FCSTD DOCUMENT  (FreeCAD 1.0R38643 (Git))
Label: Acryl01
License: All rights reserved
LicenseURL: https://en.wikipedia.org/wiki/All_rights_reserved
objects: Sketcher::SketchObject×1, PartDesign::Body×1
note: 3 computed .brp shape members not serialized (recipe doc carries the construction recipe); baked Part::Feature solids carry a one-line shape summary decoded from their .brp

FEATURE [Sketcher::SketchObject] Sketch
  ArcFitTolerance = 1e-06
  AttachmentSupport = -> [XY_Plane]
  FullyConstrained = false
  MakeInternals = false
  MapMode = 5
  sketch-geometry (21):
    g0: LineSegment StartX=-152.14 StartY=63 StartZ=0 EndX=-152.14 EndY=12 EndZ=0
    g1: LineSegment StartX=-140.14 StartY=0 StartZ=0 EndX=5.86047 EndY=0 EndZ=0
    g2: LineSegment StartX=17.8605 StartY=12 StartZ=0 EndX=17.8605 EndY=63 EndZ=0
    g3: LineSegment StartX=5.86047 StartY=75 StartZ=0 EndX=-140.14 EndY=75 EndZ=0
    g4: ArcOfCircle CenterX=-140.14 CenterY=63 CenterZ=0 NormalX=0 NormalY=0 NormalZ=1 AngleXU=0 Radius=12 StartAngle=1.5708 EndAngle=3.14159
    g5: ArcOfCircle CenterX=-140.14 CenterY=12 CenterZ=0 NormalX=0 NormalY=0 NormalZ=1 AngleXU=0 Radius=12 StartAngle=3.14159 EndAngle=4.71239
    g6: ArcOfCircle CenterX=5.86047 CenterY=12 CenterZ=0 NormalX=0 NormalY=0 NormalZ=1 AngleXU=0 Radius=12 StartAngle=4.71239 EndAngle=6.28319
    g7: ArcOfCircle CenterX=5.86047 CenterY=63 CenterZ=0 NormalX=0 NormalY=0 NormalZ=1 AngleXU=0 Radius=12 StartAngle=2e-16 EndAngle=1.5708
    g8: GeomPoint [constr] X=-152.14 Y=75 Z=0
    g9: GeomPoint [constr] X=17.8605 Y=0 Z=0
    g10: Circle CenterX=5.96219 CenterY=55.25 CenterZ=0 NormalX=0 NormalY=0 NormalZ=1 AngleXU=0 Radius=1.5
    g11: Circle CenterX=-65.0378 CenterY=55.25 CenterZ=0 NormalX=0 NormalY=0 NormalZ=1 AngleXU=0 Radius=1.5
    g12: Circle CenterX=-65.0378 CenterY=19.75 CenterZ=0 NormalX=0 NormalY=0 NormalZ=1 AngleXU=0 Radius=1.5
    g13: Circle CenterX=5.96219 CenterY=19.75 CenterZ=0 NormalX=0 NormalY=0 NormalZ=1 AngleXU=0 Radius=1.5
    g14: ArcOfCircle CenterX=17.8605 CenterY=37.5 CenterZ=0 NormalX=0 NormalY=0 NormalZ=1 AngleXU=0 Radius=12 StartAngle=4.71239 EndAngle=7.85398
    g15: ArcOfCircle CenterX=-12.1395 CenterY=37.5 CenterZ=0 NormalX=0 NormalY=0 NormalZ=1 AngleXU=0 Radius=12 StartAngle=1.5708 EndAngle=4.71239
    g16: LineSegment StartX=17.8605 StartY=25.5 StartZ=0 EndX=-12.1395 EndY=25.5 EndZ=0
    g17: LineSegment StartX=17.8605 StartY=49.5 StartZ=0 EndX=-12.1395 EndY=49.5 EndZ=0
    g18: LineSegment [constr] StartX=-65.0378 StartY=55.25 StartZ=0 EndX=-65.0378 EndY=19.75 EndZ=0
    g19: GeomPoint X=-65.0378 Y=37.5 Z=0
    g20: GeomPoint X=-152.14 Y=37.5 Z=0
  constraints (47):
    c: Tangent(g0,g4) = -1.5708
    c: Tangent(g0,g5) = -1.5708
    c: Tangent(g1,g5) = -1.5708
    c: Tangent(g1,g6) = -1.5708
    c: Tangent(g2,g6) = -1.5708
    c: Tangent(g2,g7) = -1.5708
    c: Tangent(g3,g7) = -1.5708
    c: Tangent(g3,g4) = -1.5708
    c: Vertical(g0)
    c: Vertical(g2)
    c: Horizontal(g1)
    c: Horizontal(g3)
    c: Equal(g4,g5)
    c: Equal(g5,g6)
    c: Equal(g6,g7)
    c: PointOnObject(g8,g0)
    c: PointOnObject(g8,g3)
    c: PointOnObject(g9,g1)
    c: PointOnObject(g9,g2)
    c: Distance(g0,g2) = 170
    c: Distance(g1,g3) = 75
    c: Radius(g5) = 12
    c: PointOnObject(g9,g-1)
    c: Diameter(g10) = 3
    c: Diameter(g11) = 3
    c: Horizontal(g10,g11)
    c: DistanceX(g11,g10) = 71
    c: Diameter(g12) = 3
    c: Diameter(g13) = 3
    c: Vertical(g12,g11)
    c: Vertical(g13,g10)
    c: Horizontal(g12,g13)
    c: DistanceY(g12,g11) = 35.5
    c: Tangent(g14,g16) = 1.5708
    c: Tangent(g14,g17) = -1.5708
    c: Tangent(g15,g16) = 1.5708
    c: Tangent(g15,g17) = -1.5708
    c: Equal(g14,g15)
    c: Distance(g14,g15) = 30
    c: Angle(g-1,g16) = 3.14159
    c: Radius(g14) = 12
    c: Symmetric(g2,g2,g14)
    c: Coincident(g18,g11)
    c: Coincident(g18,g12)
    c: Symmetric(g18,g18,g19)
    c: Symmetric(g0,g0,g20)
    c: Horizontal(g20,g19)
FEATURE [PartDesign::Body] Body
  AllowCompound = false
  Group = -> [Sketch]
  Origin = -> Origin
